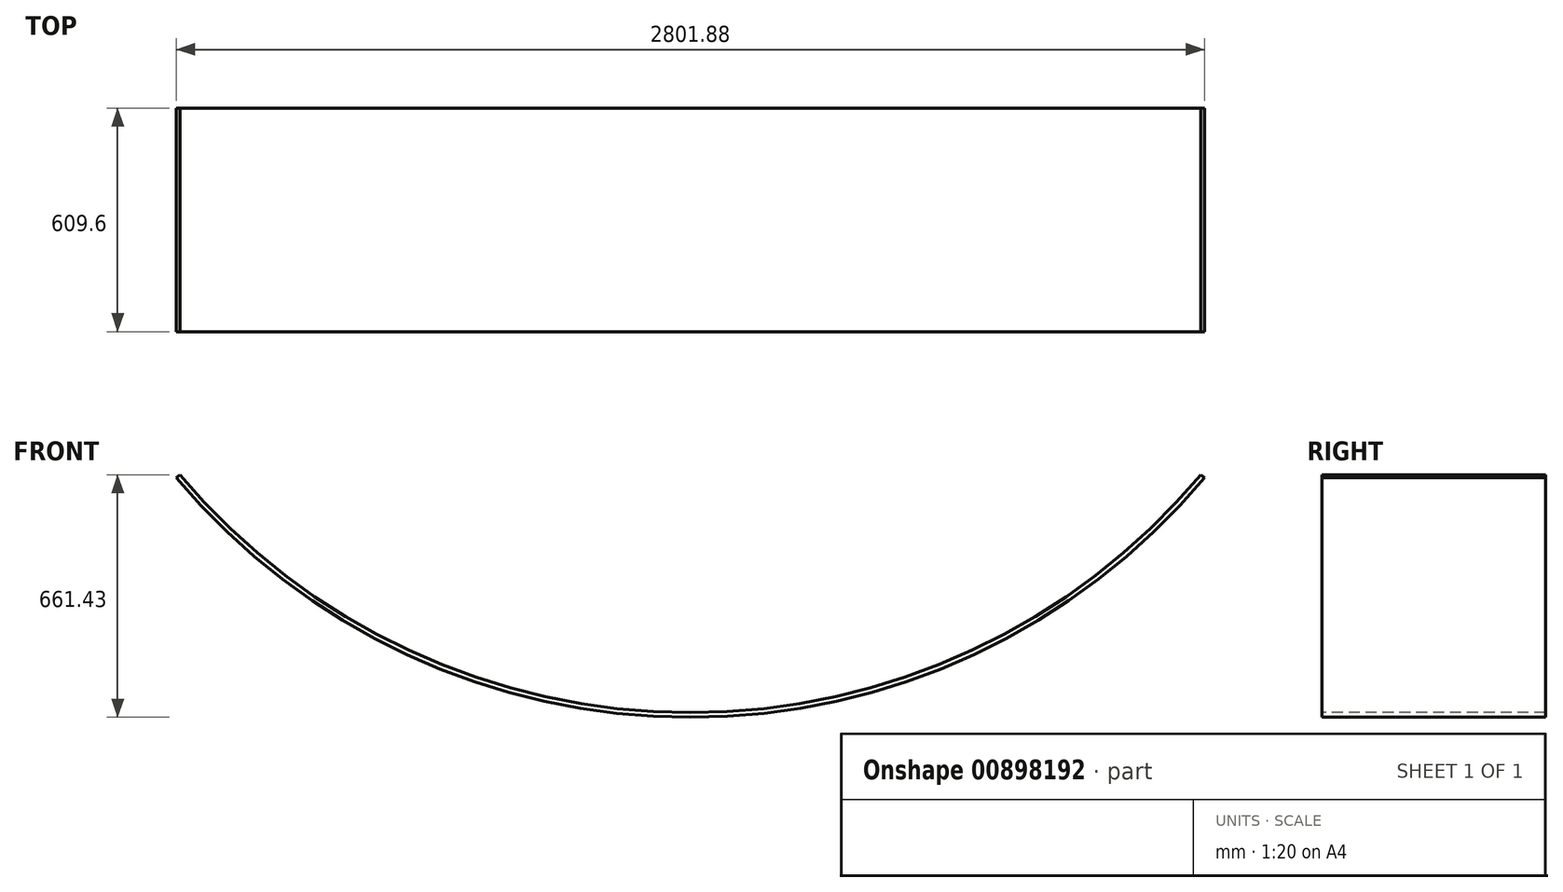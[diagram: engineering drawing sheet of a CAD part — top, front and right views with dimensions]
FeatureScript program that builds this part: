
annotation { "Feature Type Name" : "Feature", "Feature Type Description" : "" }
export const myFeature = defineFeature(function(context is Context, id is Id, definition is map)
    precondition{}
    {
        {
            var Q0;
            Q0=qCreatedBy(makeId("Front.planeOp"),FACE);
            var sketch = newSketch(context, id + "F0", { "sketchPlane" : qUnion([Q0])});
            skArc(sketch, "E0", {"start": v(-1400.94, -1175.53) * mm, "mid": v(0, -1828.8) * mm, "end": v(1400.94, -1175.53) * mm});
            skArc(sketch, "E1", {"start": v(-1391.21, -1167.37) * mm, "mid": v(0, -1816.1) * mm, "end": v(1391.21, -1167.37) * mm});
            skLineSegment(sketch, "E2", {"start": v(0, 0) * mm, "end": v(-1400.94, -1175.53) * mm});
            skLineSegment(sketch, "E3", {"start": v(0, 0) * mm, "end": v(0, -1828.8) * mm});
            skLineSegment(sketch, "E4", {"start": v(0, 0) * mm, "end": v(1400.94, -1175.53) * mm});
            skSolve(sketch);
        }
        {
            var Q0;
            {var subQ0=sQuery(id+"F0.wireOp",EDGE,"E2");var subQ1=sQuery(id+"F0.wireOp",EDGE,"E0");var subQ2=makeQuery(id+"F0.imprint","INTERSECT",VERTEX,{"derivedFrom":[subQ1,subQ0]});Q0=makeQuery(id+"F0.imprint","IMPRINT",FACE,{"disambiguationData":[TD([[makeQuery(id+"F0.imprint","IMPRINT",EDGE,{"disambiguationData":[TD([[subQ2,-1.0]])],"derivedFrom":subQ1}),1.0]])]});}
            var Q1;
            {var subQ0=sQuery(id+"F0.wireOp",EDGE,"E4");var subQ1=sQuery(id+"F0.wireOp",EDGE,"E0");var subQ2=makeQuery(id+"F0.imprint","INTERSECT",VERTEX,{"derivedFrom":[subQ1,subQ0]});Q1=makeQuery(id+"F0.imprint","IMPRINT",FACE,{"disambiguationData":[TD([[makeQuery(id+"F0.imprint","IMPRINT",EDGE,{"disambiguationData":[TD([[subQ2,1.0]])],"derivedFrom":subQ1}),1.0]])]});}
            extrude(context, id + "F1", {"entities" : qUnion([Q0, Q1]), "oppositeDirection" : true, "depth" : 609.6 * mm, "offsetDistance" : 25.4 * mm});
        }
    });
